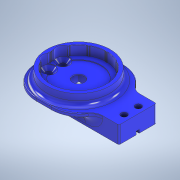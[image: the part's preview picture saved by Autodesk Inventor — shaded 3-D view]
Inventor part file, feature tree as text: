
AUTODESK INVENTOR PART (.ipt)
format: ipt  version: 2022 (Build 260153000, 153)  size: 1,370,624 bytes
history: native  units: mm
features: projected_geometry x17, extrude x13, sketch x12, fillet x8, other x6, pattern_circular x2, chamfer x1, revolve x1, mirror x1
ambient origin geometry x8: Origin, YZ Plane, XZ Plane, XY Plane, X Axis, Y Axis, Z Axis, Center Point
bodies: Body1 (feature_tree)
feature tree (61):
  other  "Твердое тело1"
  extrude  "Выдавливание1"  Depth=21.5mm
  extrude  "Выдавливание2"  Depth=41.0mm
  extrude  "Выдавливание3"  Depth=59.0mm
  extrude  "Выдавливание4"  Depth=10.6mm TaperAngle=0.0deg
  extrude  "Выдавливание5"  Depth=2.0mm
  extrude  "Выдавливание6"  Depth=4.4mm
  fillet  "Сопряжение1"  Radius=10600.0mm
  fillet  "Сопряжение2"  Radius=14.3mm
  fillet  "Сопряжение3"  Radius=10.0mm
  fillet  "Сопряжение4"  Radius=0.9mm
  extrude  "Выдавливание8"  Depth=150.0mm TaperAngle=0.0deg
  fillet  "Сопряжение6"  Radius=37.3mm
  other  "РабОсь1"
  fillet  "Сопряжение8"  Radius=2.5mm
  pattern_circular  "Круговой массив1"  [2 undecoded]
  extrude  "Выдавливание9"  Depth=3.0mm
  extrude  "Выдавливание10"  Depth=2.5mm TaperAngle=0.0deg
  fillet  "Сопряжение9"  Radius=20.0mm
  extrude  "Выдавливание11"  Depth=3.0mm
  chamfer  "Фаска1"  Distance=0.5mm
  extrude  "Выдавливание12"  Depth=1.0mm
  other  "РабОсь2"
  other  "РабПлоскость1"
  sketch  "Эскиз14"
  fillet  "Сопряжение11"  Radius=25.0mm
  extrude  "Выдавливание15"  Depth=0.7mm
  pattern_circular  "Круговой массив3"  Count=12 Angle=360.0deg
  revolve  "Вращение2"
  other  "РабПлоскость2"
  mirror  "Зеркальное отражение1"
  extrude  "Выдавливание17"  Depth=5.0mm TaperAngle=0.0deg
  sketch  "Эскиз1"
  sketch  "Эскиз2"
  sketch  "Эскиз3"
  projected_geometry  "Спроецированная петля1"
  sketch  "Эскиз5"
  projected_geometry  "Спроецированная петля2"
  sketch  "Эскиз6"
  projected_geometry  "Спроецированная петля3"
  projected_geometry  "Спроецированная петля4"
  projected_geometry  "Спроецированная петля5"
  sketch  "Эскиз9"
  sketch  "Эскиз10"
  projected_geometry  "Спроецированная петля6"
  sketch  "Эскиз12"
  projected_geometry  "Спроецированная петля7"
  projected_geometry  "Спроецированная петля8"
  sketch  "Эскиз13"
  other  "РабОсь3"
  sketch  "Эскиз17"
  projected_geometry  "Спроецированная петля9"
  projected_geometry  "Спроецированная петля10"
  projected_geometry  "Спроецированная петля11"
  projected_geometry  "Спроецированная петля12"
  projected_geometry  "Спроецированная петля13"
  projected_geometry  "Спроецированная петля14"
  projected_geometry  "Спроецированная петля15"
  projected_geometry  "Спроецированная петля16"
  sketch  "Эскиз18"
  projected_geometry  "Спроецированная петля17"
note: 2 required parameter values undecoded (feature->parameter linkage not recoverable at this tier; creation-order binding heuristic only, values carry confidence <= 0.55)
